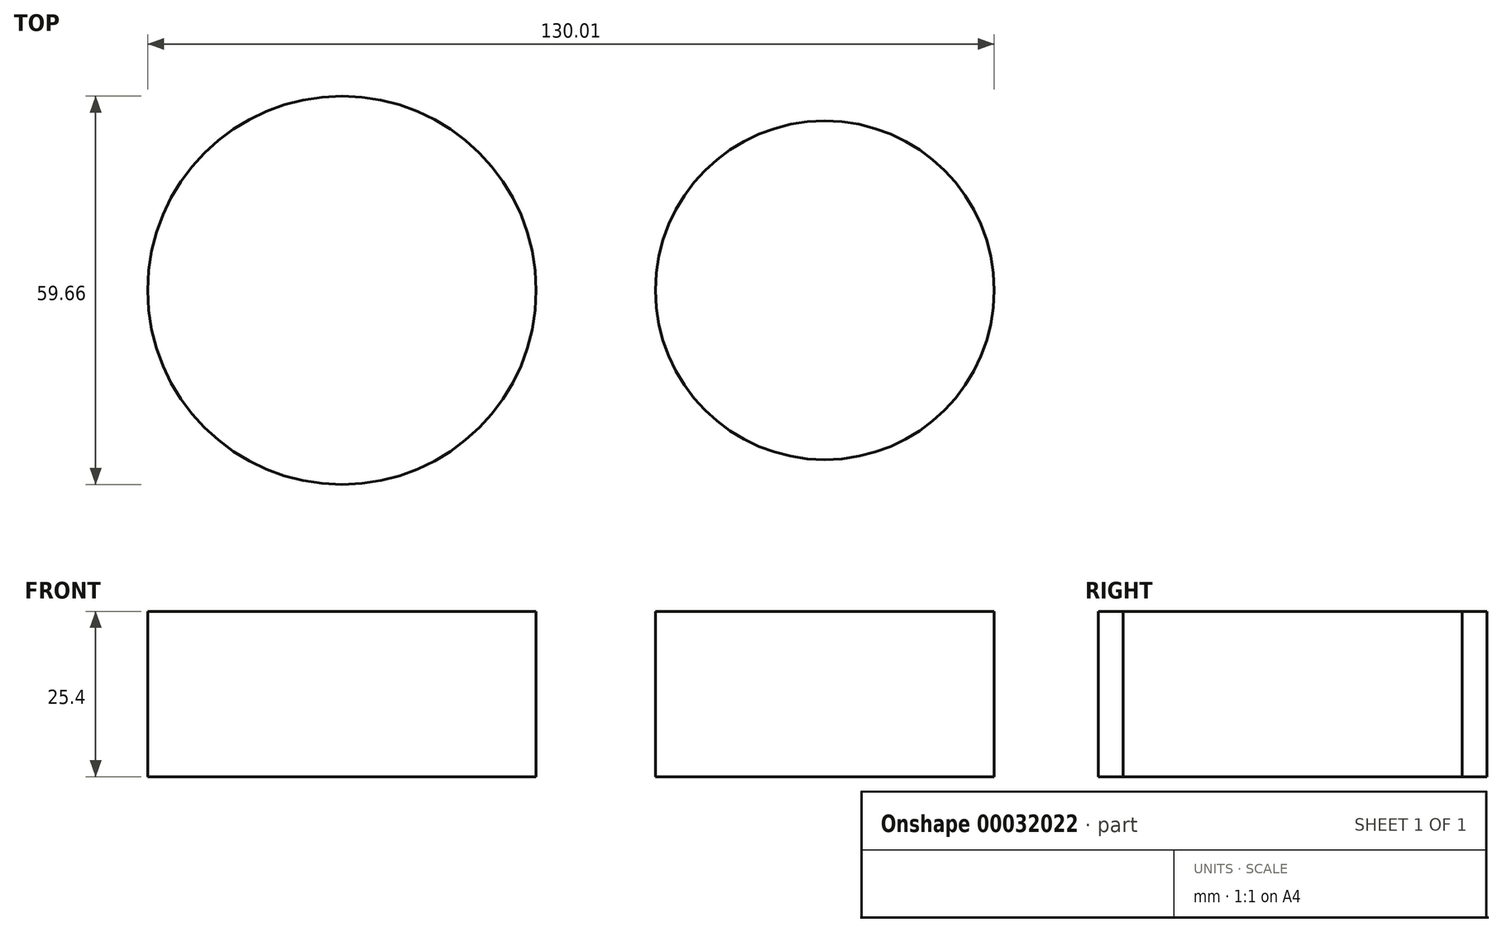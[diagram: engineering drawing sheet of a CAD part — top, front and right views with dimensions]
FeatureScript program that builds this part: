
annotation { "Feature Type Name" : "Feature", "Feature Type Description" : "" }
export const myFeature = defineFeature(function(context is Context, id is Id, definition is map)
    precondition{}
    {
        {
            var Q0;
            Q0=qCreatedBy(makeId("Top.planeOp"),FACE);
            var sketch = newSketch(context, id + "F0", { "sketchPlane" : qUnion([Q0])});
            skCircle(sketch, "E0", {"center": v(-39.73, 0) * mm, "radius": 29.83 * mm});
            skCircle(sketch, "E1", {"center": v(34.43, 0) * mm, "radius": 26.02 * mm});
            skSolve(sketch);
        }
        {
            var Q0;
            Q0=makeQuery(id+"F0.imprint","IMPRINT",FACE,{"disambiguationData":[TD([[makeQuery(id+"F0.imprint","IMPRINT",EDGE,{"derivedFrom":sQuery(id+"F0.wireOp",EDGE,"E0")}),1.0]])]});
            var Q1;
            Q1=makeQuery(id+"F0.imprint","IMPRINT",FACE,{"disambiguationData":[TD([[makeQuery(id+"F0.imprint","IMPRINT",EDGE,{"derivedFrom":sQuery(id+"F0.wireOp",EDGE,"E1")}),1.0]])]});
            extrude(context, id + "F1", {"entities" : qUnion([Q0, Q1]), "depth" : 25.4 * mm});
        }
    });
